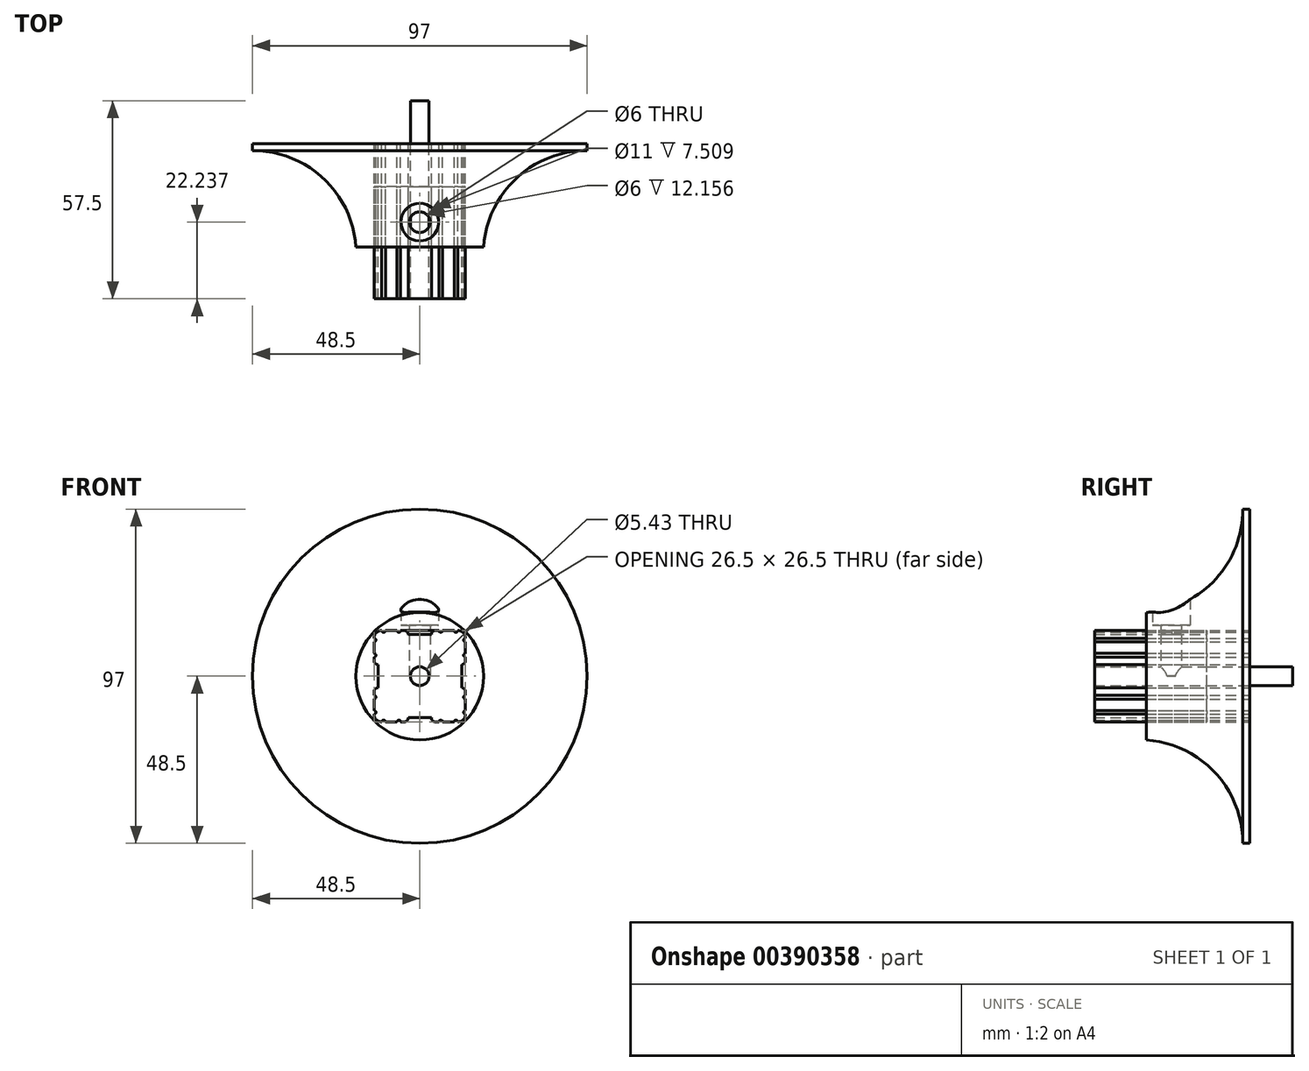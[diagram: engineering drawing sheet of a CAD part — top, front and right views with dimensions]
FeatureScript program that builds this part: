
annotation { "Feature Type Name" : "Feature", "Feature Type Description" : "" }
export const myFeature = defineFeature(function(context is Context, id is Id, definition is map)
    precondition{}
    {
        {
            var Q0;
            Q0=qCreatedBy(makeId("Front.planeOp"),FACE);
            var sketch = newSketch(context, id + "F0", { "sketchPlane" : qUnion([Q0])});
            skCircle(sketch, "E0", {"center": v(0, 0) * mm, "radius": 2.72 * mm});
            skArc(sketch, "E1", {"start": v(-1.78, -4.7) * mm, "mid": v(-3.05, -4.94) * mm, "end": v(-4.12, -5.66) * mm});
            skLineSegment(sketch, "E2", {"start": v(-1.78, -4.7) * mm, "end": v(1.78, -4.7) * mm});
            skArc(sketch, "E3", {"start": v(4.12, -5.66) * mm, "mid": v(3.05, -4.94) * mm, "end": v(1.78, -4.7) * mm});
            skLineSegment(sketch, "E4", {"start": v(4.12, -5.66) * mm, "end": v(7.5, -9.02) * mm});
            skArc(sketch, "E5", {"start": v(6.7, -10.94) * mm, "mid": v(7.74, -10.25) * mm, "end": v(7.5, -9.02) * mm});
            skLineSegment(sketch, "E6", {"start": v(6.7, -10.94) * mm, "end": v(4.47, -10.94) * mm});
            skArc(sketch, "E7", {"start": v(4.47, -10.94) * mm, "mid": v(3.7, -11.27) * mm, "end": v(3.38, -12.04) * mm});
            skLineSegment(sketch, "E8", {"start": v(3.38, -12.04) * mm, "end": v(3.38, -12.16) * mm});
            skArc(sketch, "E9", {"start": v(3.38, -12.16) * mm, "mid": v(3.7, -12.93) * mm, "end": v(4.47, -13.25) * mm});
            skLineSegment(sketch, "E10", {"start": v(4.47, -13.25) * mm, "end": v(5.55, -13.25) * mm});
            skArc(sketch, "E11", {"start": v(6.6, -13.25) * mm, "mid": v(6.08, -12.72) * mm, "end": v(5.55, -13.25) * mm});
            skLineSegment(sketch, "E12", {"start": v(6.6, -13.25) * mm, "end": v(9.96, -13.25) * mm});
            skArc(sketch, "E13", {"start": v(11.02, -13.25) * mm, "mid": v(10.5, -12.72) * mm, "end": v(9.96, -13.25) * mm});
            skArc(sketch, "E14", {"start": v(11.02, -13.25) * mm, "mid": v(12.6, -12.6) * mm, "end": v(13.25, -11.02) * mm});
            skArc(sketch, "E15", {"start": v(13.25, -9.96) * mm, "mid": v(12.72, -10.5) * mm, "end": v(13.25, -11.02) * mm});
            skLineSegment(sketch, "E16", {"start": v(13.25, -9.96) * mm, "end": v(13.25, -6.6) * mm});
            skArc(sketch, "E17", {"start": v(13.25, -5.55) * mm, "mid": v(12.72, -6.08) * mm, "end": v(13.25, -6.6) * mm});
            skLineSegment(sketch, "E18", {"start": v(13.25, -5.55) * mm, "end": v(13.25, -4.47) * mm});
            skArc(sketch, "E19", {"start": v(13.25, -4.47) * mm, "mid": v(12.93, -3.7) * mm, "end": v(12.16, -3.38) * mm});
            skLineSegment(sketch, "E20", {"start": v(12.16, -3.38) * mm, "end": v(12.04, -3.38) * mm});
            skArc(sketch, "E21", {"start": v(12.04, -3.38) * mm, "mid": v(11.27, -3.7) * mm, "end": v(10.94, -4.47) * mm});
            skLineSegment(sketch, "E22", {"start": v(10.94, -4.47) * mm, "end": v(10.94, -6.68) * mm});
            skArc(sketch, "E23", {"start": v(9.12, -7.44) * mm, "mid": v(10.28, -7.67) * mm, "end": v(10.94, -6.68) * mm});
            skLineSegment(sketch, "E24", {"start": v(9.12, -7.44) * mm, "end": v(5.68, -4) * mm});
            skArc(sketch, "E25", {"start": v(4.7, -1.66) * mm, "mid": v(4.96, -2.93) * mm, "end": v(5.68, -4) * mm});
            skLineSegment(sketch, "E26", {"start": v(4.7, -1.66) * mm, "end": v(4.7, 1.66) * mm});
            skArc(sketch, "E27", {"start": v(5.68, 4) * mm, "mid": v(4.96, 2.93) * mm, "end": v(4.7, 1.66) * mm});
            skLineSegment(sketch, "E28", {"start": v(5.68, 4) * mm, "end": v(9.12, 7.44) * mm});
            skArc(sketch, "E29", {"start": v(10.94, 6.68) * mm, "mid": v(10.28, 7.67) * mm, "end": v(9.12, 7.44) * mm});
            skLineSegment(sketch, "E30", {"start": v(10.94, 6.68) * mm, "end": v(10.94, 4.47) * mm});
            skArc(sketch, "E31", {"start": v(10.94, 4.47) * mm, "mid": v(11.27, 3.7) * mm, "end": v(12.04, 3.38) * mm});
            skLineSegment(sketch, "E32", {"start": v(12.04, 3.38) * mm, "end": v(12.16, 3.38) * mm});
            skArc(sketch, "E33", {"start": v(12.16, 3.38) * mm, "mid": v(12.93, 3.7) * mm, "end": v(13.25, 4.47) * mm});
            skLineSegment(sketch, "E34", {"start": v(13.25, 4.47) * mm, "end": v(13.25, 5.55) * mm});
            skArc(sketch, "E35", {"start": v(13.25, 6.6) * mm, "mid": v(12.72, 6.08) * mm, "end": v(13.25, 5.55) * mm});
            skLineSegment(sketch, "E36", {"start": v(13.25, 6.6) * mm, "end": v(13.25, 9.96) * mm});
            skArc(sketch, "E37", {"start": v(13.25, 11.02) * mm, "mid": v(12.72, 10.5) * mm, "end": v(13.25, 9.96) * mm});
            skArc(sketch, "E38", {"start": v(13.25, 11.02) * mm, "mid": v(12.6, 12.6) * mm, "end": v(11.02, 13.25) * mm});
            skArc(sketch, "E39", {"start": v(9.96, 13.25) * mm, "mid": v(10.5, 12.72) * mm, "end": v(11.02, 13.25) * mm});
            skLineSegment(sketch, "E40", {"start": v(9.96, 13.25) * mm, "end": v(6.6, 13.25) * mm});
            skArc(sketch, "E41", {"start": v(5.55, 13.25) * mm, "mid": v(6.08, 12.72) * mm, "end": v(6.6, 13.25) * mm});
            skLineSegment(sketch, "E42", {"start": v(5.55, 13.25) * mm, "end": v(4.47, 13.25) * mm});
            skArc(sketch, "E43", {"start": v(4.47, 13.25) * mm, "mid": v(3.7, 12.93) * mm, "end": v(3.38, 12.16) * mm});
            skLineSegment(sketch, "E44", {"start": v(3.38, 12.16) * mm, "end": v(3.38, 12.04) * mm});
            skArc(sketch, "E45", {"start": v(3.38, 12.04) * mm, "mid": v(3.7, 11.27) * mm, "end": v(4.47, 10.94) * mm});
            skLineSegment(sketch, "E46", {"start": v(4.47, 10.94) * mm, "end": v(6.76, 10.94) * mm});
            skArc(sketch, "E47", {"start": v(7.52, 9.1) * mm, "mid": v(7.75, 10.28) * mm, "end": v(6.76, 10.94) * mm});
            skLineSegment(sketch, "E48", {"start": v(7.52, 9.1) * mm, "end": v(4.07, 5.66) * mm});
            skArc(sketch, "E49", {"start": v(1.73, 4.7) * mm, "mid": v(3, 4.94) * mm, "end": v(4.07, 5.66) * mm});
            skLineSegment(sketch, "E50", {"start": v(1.73, 4.7) * mm, "end": v(-1.73, 4.7) * mm});
            skArc(sketch, "E51", {"start": v(-4.07, 5.66) * mm, "mid": v(-3, 4.94) * mm, "end": v(-1.73, 4.7) * mm});
            skLineSegment(sketch, "E52", {"start": v(-4.07, 5.66) * mm, "end": v(-7.52, 9.1) * mm});
            skArc(sketch, "E53", {"start": v(-6.76, 10.94) * mm, "mid": v(-7.75, 10.28) * mm, "end": v(-7.52, 9.1) * mm});
            skLineSegment(sketch, "E54", {"start": v(-6.76, 10.94) * mm, "end": v(-4.47, 10.94) * mm});
            skArc(sketch, "E55", {"start": v(-4.47, 10.94) * mm, "mid": v(-3.7, 11.27) * mm, "end": v(-3.38, 12.04) * mm});
            skLineSegment(sketch, "E56", {"start": v(-3.38, 12.04) * mm, "end": v(-3.38, 12.16) * mm});
            skArc(sketch, "E57", {"start": v(-3.38, 12.16) * mm, "mid": v(-3.7, 12.93) * mm, "end": v(-4.47, 13.25) * mm});
            skLineSegment(sketch, "E58", {"start": v(-4.47, 13.25) * mm, "end": v(-5.55, 13.25) * mm});
            skArc(sketch, "E59", {"start": v(-6.6, 13.25) * mm, "mid": v(-6.08, 12.72) * mm, "end": v(-5.55, 13.25) * mm});
            skLineSegment(sketch, "E60", {"start": v(-6.6, 13.25) * mm, "end": v(-9.96, 13.25) * mm});
            skArc(sketch, "E61", {"start": v(-11.02, 13.25) * mm, "mid": v(-10.5, 12.72) * mm, "end": v(-9.96, 13.25) * mm});
            skArc(sketch, "E62", {"start": v(-11.02, 13.25) * mm, "mid": v(-12.6, 12.6) * mm, "end": v(-13.25, 11.02) * mm});
            skArc(sketch, "E63", {"start": v(-13.25, 9.96) * mm, "mid": v(-12.72, 10.5) * mm, "end": v(-13.25, 11.02) * mm});
            skLineSegment(sketch, "E64", {"start": v(-13.25, 9.96) * mm, "end": v(-13.25, 6.6) * mm});
            skArc(sketch, "E65", {"start": v(-13.25, 5.55) * mm, "mid": v(-12.72, 6.08) * mm, "end": v(-13.25, 6.6) * mm});
            skLineSegment(sketch, "E66", {"start": v(-13.25, 5.55) * mm, "end": v(-13.25, 4.47) * mm});
            skArc(sketch, "E67", {"start": v(-13.25, 4.47) * mm, "mid": v(-12.93, 3.7) * mm, "end": v(-12.16, 3.38) * mm});
            skLineSegment(sketch, "E68", {"start": v(-12.16, 3.38) * mm, "end": v(-12.04, 3.38) * mm});
            skArc(sketch, "E69", {"start": v(-12.04, 3.38) * mm, "mid": v(-11.27, 3.7) * mm, "end": v(-10.94, 4.47) * mm});
            skLineSegment(sketch, "E70", {"start": v(-10.94, 4.47) * mm, "end": v(-10.94, 6.68) * mm});
            skArc(sketch, "E71", {"start": v(-9.12, 7.44) * mm, "mid": v(-10.28, 7.67) * mm, "end": v(-10.94, 6.68) * mm});
            skLineSegment(sketch, "E72", {"start": v(-9.12, 7.44) * mm, "end": v(-5.68, 4) * mm});
            skArc(sketch, "E73", {"start": v(-4.7, 1.66) * mm, "mid": v(-4.96, 2.93) * mm, "end": v(-5.68, 4) * mm});
            skLineSegment(sketch, "E74", {"start": v(-4.7, 1.66) * mm, "end": v(-4.7, -1.66) * mm});
            skArc(sketch, "E75", {"start": v(-5.68, -4) * mm, "mid": v(-4.96, -2.93) * mm, "end": v(-4.7, -1.66) * mm});
            skLineSegment(sketch, "E76", {"start": v(-5.68, -4) * mm, "end": v(-9.12, -7.44) * mm});
            skArc(sketch, "E77", {"start": v(-10.94, -6.68) * mm, "mid": v(-10.28, -7.67) * mm, "end": v(-9.12, -7.44) * mm});
            skLineSegment(sketch, "E78", {"start": v(-10.94, -6.68) * mm, "end": v(-10.94, -4.47) * mm});
            skArc(sketch, "E79", {"start": v(-10.94, -4.47) * mm, "mid": v(-11.27, -3.7) * mm, "end": v(-12.04, -3.38) * mm});
            skLineSegment(sketch, "E80", {"start": v(-12.04, -3.38) * mm, "end": v(-12.16, -3.38) * mm});
            skArc(sketch, "E81", {"start": v(-12.16, -3.38) * mm, "mid": v(-12.93, -3.7) * mm, "end": v(-13.25, -4.47) * mm});
            skLineSegment(sketch, "E82", {"start": v(-13.25, -4.47) * mm, "end": v(-13.25, -5.55) * mm});
            skArc(sketch, "E83", {"start": v(-13.25, -6.6) * mm, "mid": v(-12.72, -6.08) * mm, "end": v(-13.25, -5.55) * mm});
            skLineSegment(sketch, "E84", {"start": v(-13.25, -6.6) * mm, "end": v(-13.25, -9.96) * mm});
            skArc(sketch, "E85", {"start": v(-13.25, -11.02) * mm, "mid": v(-12.72, -10.5) * mm, "end": v(-13.25, -9.96) * mm});
            skArc(sketch, "E86", {"start": v(-13.25, -11.02) * mm, "mid": v(-12.6, -12.6) * mm, "end": v(-11.02, -13.25) * mm});
            skArc(sketch, "E87", {"start": v(-9.96, -13.25) * mm, "mid": v(-10.5, -12.72) * mm, "end": v(-11.02, -13.25) * mm});
            skLineSegment(sketch, "E88", {"start": v(-9.96, -13.25) * mm, "end": v(-6.6, -13.25) * mm});
            skArc(sketch, "E89", {"start": v(-5.55, -13.25) * mm, "mid": v(-6.08, -12.72) * mm, "end": v(-6.6, -13.25) * mm});
            skLineSegment(sketch, "E90", {"start": v(-5.55, -13.25) * mm, "end": v(-4.47, -13.25) * mm});
            skArc(sketch, "E91", {"start": v(-4.47, -13.25) * mm, "mid": v(-3.7, -12.93) * mm, "end": v(-3.38, -12.16) * mm});
            skLineSegment(sketch, "E92", {"start": v(-3.38, -12.16) * mm, "end": v(-3.38, -12.04) * mm});
            skArc(sketch, "E93", {"start": v(-3.38, -12.04) * mm, "mid": v(-3.7, -11.27) * mm, "end": v(-4.47, -10.94) * mm});
            skLineSegment(sketch, "E94", {"start": v(-4.47, -10.94) * mm, "end": v(-6.7, -10.94) * mm});
            skArc(sketch, "E95", {"start": v(-7.5, -9.02) * mm, "mid": v(-7.74, -10.25) * mm, "end": v(-6.7, -10.94) * mm});
            skLineSegment(sketch, "E96", {"start": v(-7.5, -9.02) * mm, "end": v(-4.12, -5.66) * mm});
            skLineSegment(sketch, "E97", {"start": v(-12.04, 3.38) * mm, "end": v(-12.04, -4.47) * mm});
            skLineSegment(sketch, "E98", {"start": v(-3.38, -12.04) * mm, "end": v(3.38, -12.04) * mm});
            skLineSegment(sketch, "E99", {"start": v(12.16, -3.38) * mm, "end": v(12.16, 3.38) * mm});
            skLineSegment(sketch, "E100", {"start": v(3.38, 12.16) * mm, "end": v(-3.38, 12.16) * mm});
            skSolve(sketch);
        }
        {
            var Q0;
            Q0=qCreatedBy(makeId("Front.planeOp"),FACE);
            var sketch = newSketch(context, id + "F1", { "sketchPlane" : qUnion([Q0])});
            skCircle(sketch, "E101", {"center": v(0, 0) * mm, "radius": 18.5 * mm});
            skCircle(sketch, "E102", {"center": v(0, 0) * mm, "radius": 48.5 * mm});
            skSolve(sketch);
        }
        {
            var Q0;
            Q0 = qSketchRegion(id + "F1", true);
            var Q1;
            Q1=makeQuery(id+"F1.imprint","IMPRINT",FACE,{"disambiguationData":[TD([[makeQuery(id+"F1.imprint","IMPRINT",EDGE,{"derivedFrom":sQuery(id+"F1.wireOp",EDGE,"E101")}),1.0]])]});
            extrude(context, id + "F2", {"entities" : qUnion([Q0, Q1]), "depth" : 2 * mm});
        }
        {
            var Q0;
            Q0=makeQuery(id+"F1.imprint","IMPRINT",FACE,{"disambiguationData":[TD([[makeQuery(id+"F1.imprint","IMPRINT",EDGE,{"derivedFrom":sQuery(id+"F1.wireOp",EDGE,"E101")}),1.0]])]});
            extrude(context, id + "F3", {"entities" : qUnion([Q0]), "operationType" : NewBodyOperationType.ADD, "depth" : 30 * mm});
        }
        {
            var Q0;
            Q0=makeQuery(id+"F3.boolean.opBoolean","INTERSECT",EDGE,{"derivedFrom":[makeQuery(id+"F2.opExtrude","CAP_FACE",FACE,{"disambiguationData":[OSD([sQuery(id+"F1.wireOp",EDGE,"E102")])],"isStart":false}),makeQuery(id+"F3.opExtrude","SWEPT_FACE",FACE,{"disambiguationData":[OSD([sQuery(id+"F1.wireOp",EDGE,"E101")])]})]});
            fillet(context, id + "F4", {"entities" : qUnion([Q0]), "radius" : 30 * mm, "tangentPropagation" : true, "allowEdgeOverflow" : false});
        }
        {
            var Q0;
            Q0=makeQuery(id+"F1.imprint","IMPRINT",FACE,{"disambiguationData":[TD([[makeQuery(id+"F1.imprint","IMPRINT",EDGE,{"derivedFrom":sQuery(id+"F1.wireOp",EDGE,"E101")}),-1.0]])]});
            var sketch = newSketch(context, id + "F5", { "sketchPlane" : qUnion([Q0])});
            skArc(sketch, "E103.0.0", {"start": v(-6.7, -10.94) * mm, "mid": v(-7.74, -10.25) * mm, "end": v(-7.5, -9.02) * mm});
            skLineSegment(sketch, "E103.0.1", {"start": v(-7.5, -9.02) * mm, "end": v(-4.12, -5.66) * mm});
            skArc(sketch, "E103.0.2", {"start": v(-4.12, -5.66) * mm, "mid": v(-3.05, -4.94) * mm, "end": v(-1.78, -4.7) * mm});
            skLineSegment(sketch, "E103.0.3", {"start": v(-1.78, -4.7) * mm, "end": v(1.78, -4.7) * mm});
            skArc(sketch, "E103.0.4", {"start": v(1.78, -4.7) * mm, "mid": v(3.05, -4.94) * mm, "end": v(4.12, -5.66) * mm});
            skLineSegment(sketch, "E103.0.5", {"start": v(4.12, -5.66) * mm, "end": v(7.5, -9.02) * mm});
            skArc(sketch, "E103.0.6", {"start": v(7.5, -9.02) * mm, "mid": v(7.74, -10.25) * mm, "end": v(6.7, -10.94) * mm});
            skLineSegment(sketch, "E103.0.7", {"start": v(6.7, -10.94) * mm, "end": v(4.47, -10.94) * mm});
            skArc(sketch, "E103.0.8", {"start": v(4.47, -10.94) * mm, "mid": v(3.7, -11.27) * mm, "end": v(3.38, -12.04) * mm});
            skLineSegment(sketch, "E103.0.9", {"start": v(3.38, -12.04) * mm, "end": v(3.38, -12.16) * mm});
            skArc(sketch, "E103.0.10", {"start": v(3.38, -12.16) * mm, "mid": v(3.7, -12.93) * mm, "end": v(4.47, -13.25) * mm});
            skLineSegment(sketch, "E103.0.11", {"start": v(4.47, -13.25) * mm, "end": v(5.55, -13.25) * mm});
            skArc(sketch, "E103.0.12", {"start": v(5.55, -13.25) * mm, "mid": v(6.08, -12.72) * mm, "end": v(6.6, -13.25) * mm});
            skLineSegment(sketch, "E103.0.13", {"start": v(6.6, -13.25) * mm, "end": v(9.96, -13.25) * mm});
            skArc(sketch, "E103.0.14", {"start": v(9.96, -13.25) * mm, "mid": v(10.5, -12.72) * mm, "end": v(11.02, -13.25) * mm});
            skArc(sketch, "E103.0.15", {"start": v(11.02, -13.25) * mm, "mid": v(12.6, -12.6) * mm, "end": v(13.25, -11.02) * mm});
            skArc(sketch, "E103.0.16", {"start": v(13.25, -11.02) * mm, "mid": v(12.72, -10.5) * mm, "end": v(13.25, -9.96) * mm});
            skLineSegment(sketch, "E103.0.17", {"start": v(13.25, -9.96) * mm, "end": v(13.25, -6.6) * mm});
            skArc(sketch, "E103.0.18", {"start": v(13.25, -6.6) * mm, "mid": v(12.72, -6.08) * mm, "end": v(13.25, -5.55) * mm});
            skLineSegment(sketch, "E103.0.19", {"start": v(13.25, -5.55) * mm, "end": v(13.25, -4.47) * mm});
            skArc(sketch, "E103.0.20", {"start": v(13.25, -4.47) * mm, "mid": v(12.93, -3.7) * mm, "end": v(12.16, -3.38) * mm});
            skLineSegment(sketch, "E103.0.21", {"start": v(12.16, -3.38) * mm, "end": v(12.04, -3.38) * mm});
            skArc(sketch, "E103.0.22", {"start": v(12.04, -3.38) * mm, "mid": v(11.27, -3.7) * mm, "end": v(10.94, -4.47) * mm});
            skLineSegment(sketch, "E103.0.23", {"start": v(10.94, -4.47) * mm, "end": v(10.94, -6.68) * mm});
            skArc(sketch, "E103.0.24", {"start": v(10.94, -6.68) * mm, "mid": v(10.28, -7.67) * mm, "end": v(9.12, -7.44) * mm});
            skLineSegment(sketch, "E103.0.25", {"start": v(9.12, -7.44) * mm, "end": v(5.68, -4) * mm});
            skArc(sketch, "E103.0.26", {"start": v(5.68, -4) * mm, "mid": v(4.96, -2.93) * mm, "end": v(4.7, -1.66) * mm});
            skLineSegment(sketch, "E103.0.27", {"start": v(4.7, -1.66) * mm, "end": v(4.7, 1.66) * mm});
            skArc(sketch, "E103.0.28", {"start": v(4.7, 1.66) * mm, "mid": v(4.96, 2.93) * mm, "end": v(5.68, 4) * mm});
            skLineSegment(sketch, "E103.0.29", {"start": v(5.68, 4) * mm, "end": v(9.12, 7.44) * mm});
            skArc(sketch, "E103.0.30", {"start": v(9.12, 7.44) * mm, "mid": v(10.28, 7.67) * mm, "end": v(10.94, 6.68) * mm});
            skLineSegment(sketch, "E103.0.31", {"start": v(10.94, 6.68) * mm, "end": v(10.94, 4.47) * mm});
            skArc(sketch, "E103.0.32", {"start": v(10.94, 4.47) * mm, "mid": v(11.27, 3.7) * mm, "end": v(12.04, 3.38) * mm});
            skLineSegment(sketch, "E103.0.33", {"start": v(12.04, 3.38) * mm, "end": v(12.16, 3.38) * mm});
            skArc(sketch, "E103.0.34", {"start": v(12.16, 3.38) * mm, "mid": v(12.93, 3.7) * mm, "end": v(13.25, 4.47) * mm});
            skLineSegment(sketch, "E103.0.35", {"start": v(13.25, 4.47) * mm, "end": v(13.25, 5.55) * mm});
            skArc(sketch, "E103.0.36", {"start": v(13.25, 5.55) * mm, "mid": v(12.72, 6.08) * mm, "end": v(13.25, 6.6) * mm});
            skLineSegment(sketch, "E103.0.37", {"start": v(13.25, 6.6) * mm, "end": v(13.25, 9.96) * mm});
            skArc(sketch, "E103.0.38", {"start": v(13.25, 9.96) * mm, "mid": v(12.72, 10.5) * mm, "end": v(13.25, 11.02) * mm});
            skArc(sketch, "E103.0.39", {"start": v(13.25, 11.02) * mm, "mid": v(12.6, 12.6) * mm, "end": v(11.02, 13.25) * mm});
            skArc(sketch, "E103.0.40", {"start": v(11.02, 13.25) * mm, "mid": v(10.5, 12.72) * mm, "end": v(9.96, 13.25) * mm});
            skLineSegment(sketch, "E103.0.41", {"start": v(9.96, 13.25) * mm, "end": v(6.6, 13.25) * mm});
            skArc(sketch, "E103.0.42", {"start": v(6.6, 13.25) * mm, "mid": v(6.08, 12.72) * mm, "end": v(5.55, 13.25) * mm});
            skLineSegment(sketch, "E103.0.43", {"start": v(5.55, 13.25) * mm, "end": v(4.47, 13.25) * mm});
            skArc(sketch, "E103.0.44", {"start": v(4.47, 13.25) * mm, "mid": v(3.7, 12.93) * mm, "end": v(3.38, 12.16) * mm});
            skLineSegment(sketch, "E103.0.45", {"start": v(3.38, 12.16) * mm, "end": v(3.38, 12.04) * mm});
            skArc(sketch, "E103.0.46", {"start": v(3.38, 12.04) * mm, "mid": v(3.7, 11.27) * mm, "end": v(4.47, 10.94) * mm});
            skLineSegment(sketch, "E103.0.47", {"start": v(4.47, 10.94) * mm, "end": v(6.76, 10.94) * mm});
            skArc(sketch, "E103.0.48", {"start": v(6.76, 10.94) * mm, "mid": v(7.75, 10.28) * mm, "end": v(7.52, 9.1) * mm});
            skLineSegment(sketch, "E103.0.49", {"start": v(7.52, 9.1) * mm, "end": v(4.07, 5.66) * mm});
            skArc(sketch, "E103.0.50", {"start": v(4.07, 5.66) * mm, "mid": v(3, 4.94) * mm, "end": v(1.73, 4.7) * mm});
            skLineSegment(sketch, "E103.0.51", {"start": v(1.73, 4.7) * mm, "end": v(-1.73, 4.7) * mm});
            skArc(sketch, "E103.0.52", {"start": v(-1.73, 4.7) * mm, "mid": v(-3, 4.94) * mm, "end": v(-4.07, 5.66) * mm});
            skLineSegment(sketch, "E103.0.53", {"start": v(-4.07, 5.66) * mm, "end": v(-7.52, 9.1) * mm});
            skArc(sketch, "E103.0.54", {"start": v(-7.52, 9.1) * mm, "mid": v(-7.75, 10.28) * mm, "end": v(-6.76, 10.94) * mm});
            skLineSegment(sketch, "E103.0.55", {"start": v(-6.76, 10.94) * mm, "end": v(-4.47, 10.94) * mm});
            skArc(sketch, "E103.0.56", {"start": v(-4.47, 10.94) * mm, "mid": v(-3.7, 11.27) * mm, "end": v(-3.38, 12.04) * mm});
            skLineSegment(sketch, "E103.0.57", {"start": v(-3.38, 12.04) * mm, "end": v(-3.38, 12.16) * mm});
            skArc(sketch, "E103.0.58", {"start": v(-3.38, 12.16) * mm, "mid": v(-3.7, 12.93) * mm, "end": v(-4.47, 13.25) * mm});
            skLineSegment(sketch, "E103.0.59", {"start": v(-4.47, 13.25) * mm, "end": v(-5.55, 13.25) * mm});
            skArc(sketch, "E103.0.60", {"start": v(-5.55, 13.25) * mm, "mid": v(-6.08, 12.72) * mm, "end": v(-6.6, 13.25) * mm});
            skLineSegment(sketch, "E103.0.61", {"start": v(-6.6, 13.25) * mm, "end": v(-9.96, 13.25) * mm});
            skArc(sketch, "E103.0.62", {"start": v(-9.96, 13.25) * mm, "mid": v(-10.5, 12.72) * mm, "end": v(-11.02, 13.25) * mm});
            skArc(sketch, "E103.0.63", {"start": v(-11.02, 13.25) * mm, "mid": v(-12.6, 12.6) * mm, "end": v(-13.25, 11.02) * mm});
            skArc(sketch, "E103.0.64", {"start": v(-13.25, 11.02) * mm, "mid": v(-12.72, 10.5) * mm, "end": v(-13.25, 9.96) * mm});
            skLineSegment(sketch, "E103.0.65", {"start": v(-13.25, 9.96) * mm, "end": v(-13.25, 6.6) * mm});
            skArc(sketch, "E103.0.66", {"start": v(-13.25, 6.6) * mm, "mid": v(-12.72, 6.08) * mm, "end": v(-13.25, 5.55) * mm});
            skLineSegment(sketch, "E103.0.67", {"start": v(-13.25, 5.55) * mm, "end": v(-13.25, 4.47) * mm});
            skArc(sketch, "E103.0.68", {"start": v(-13.25, 4.47) * mm, "mid": v(-12.93, 3.7) * mm, "end": v(-12.16, 3.38) * mm});
            skLineSegment(sketch, "E103.0.69", {"start": v(-12.16, 3.38) * mm, "end": v(-12.04, 3.38) * mm});
            skArc(sketch, "E103.0.70", {"start": v(-12.04, 3.38) * mm, "mid": v(-11.27, 3.7) * mm, "end": v(-10.94, 4.47) * mm});
            skLineSegment(sketch, "E103.0.71", {"start": v(-10.94, 4.47) * mm, "end": v(-10.94, 6.68) * mm});
            skArc(sketch, "E103.0.72", {"start": v(-10.94, 6.68) * mm, "mid": v(-10.28, 7.67) * mm, "end": v(-9.12, 7.44) * mm});
            skLineSegment(sketch, "E103.0.73", {"start": v(-9.12, 7.44) * mm, "end": v(-5.68, 4) * mm});
            skArc(sketch, "E103.0.74", {"start": v(-5.68, 4) * mm, "mid": v(-4.96, 2.93) * mm, "end": v(-4.7, 1.66) * mm});
            skLineSegment(sketch, "E103.0.75", {"start": v(-4.7, 1.66) * mm, "end": v(-4.7, -1.66) * mm});
            skArc(sketch, "E103.0.76", {"start": v(-4.7, -1.66) * mm, "mid": v(-4.96, -2.93) * mm, "end": v(-5.68, -4) * mm});
            skLineSegment(sketch, "E103.0.77", {"start": v(-5.68, -4) * mm, "end": v(-9.12, -7.44) * mm});
            skArc(sketch, "E103.0.78", {"start": v(-9.12, -7.44) * mm, "mid": v(-10.28, -7.67) * mm, "end": v(-10.94, -6.68) * mm});
            skLineSegment(sketch, "E103.0.79", {"start": v(-10.94, -6.68) * mm, "end": v(-10.94, -4.47) * mm});
            skArc(sketch, "E103.0.80", {"start": v(-10.94, -4.47) * mm, "mid": v(-11.27, -3.7) * mm, "end": v(-12.04, -3.38) * mm});
            skLineSegment(sketch, "E103.0.81", {"start": v(-12.04, -3.38) * mm, "end": v(-12.16, -3.38) * mm});
            skArc(sketch, "E103.0.82", {"start": v(-12.16, -3.38) * mm, "mid": v(-12.93, -3.7) * mm, "end": v(-13.25, -4.47) * mm});
            skLineSegment(sketch, "E103.0.83", {"start": v(-13.25, -4.47) * mm, "end": v(-13.25, -5.55) * mm});
            skArc(sketch, "E103.0.84", {"start": v(-13.25, -5.55) * mm, "mid": v(-12.72, -6.08) * mm, "end": v(-13.25, -6.6) * mm});
            skLineSegment(sketch, "E103.0.85", {"start": v(-13.25, -6.6) * mm, "end": v(-13.25, -9.96) * mm});
            skArc(sketch, "E103.0.86", {"start": v(-13.25, -9.96) * mm, "mid": v(-12.72, -10.5) * mm, "end": v(-13.25, -11.02) * mm});
            skArc(sketch, "E103.0.87", {"start": v(-13.25, -11.02) * mm, "mid": v(-12.6, -12.6) * mm, "end": v(-11.02, -13.25) * mm});
            skArc(sketch, "E103.0.88", {"start": v(-11.02, -13.25) * mm, "mid": v(-10.5, -12.72) * mm, "end": v(-9.96, -13.25) * mm});
            skLineSegment(sketch, "E103.0.89", {"start": v(-9.96, -13.25) * mm, "end": v(-6.6, -13.25) * mm});
            skArc(sketch, "E103.0.90", {"start": v(-6.6, -13.25) * mm, "mid": v(-6.08, -12.72) * mm, "end": v(-5.55, -13.25) * mm});
            skLineSegment(sketch, "E103.0.91", {"start": v(-5.55, -13.25) * mm, "end": v(-4.47, -13.25) * mm});
            skArc(sketch, "E103.0.92", {"start": v(-4.47, -13.25) * mm, "mid": v(-3.7, -12.93) * mm, "end": v(-3.38, -12.16) * mm});
            skLineSegment(sketch, "E103.0.93", {"start": v(-3.38, -12.16) * mm, "end": v(-3.38, -12.04) * mm});
            skArc(sketch, "E103.0.94", {"start": v(-3.38, -12.04) * mm, "mid": v(-3.7, -11.27) * mm, "end": v(-4.47, -10.94) * mm});
            skLineSegment(sketch, "E103.0.95", {"start": v(-4.47, -10.94) * mm, "end": v(-6.7, -10.94) * mm});
            skLineSegment(sketch, "E104", {"start": v(4.47, 13.25) * mm, "end": v(-4.47, 13.25) * mm});
            skSolve(sketch);
        }
        {
            var Q0;
            Q0 = qSketchRegion(id + "F5", true);
            var Q1;
            {var subQ1=sQuery(id+"F0.wireOp",EDGE,"E69");Q1=makeQuery(id+"F0.imprint","IMPRINT",FACE,{"disambiguationData":[TD([[makeQuery(id+"F0.imprint","IMPRINT",EDGE,{"derivedFrom":subQ1}),-1.0]])]});}
            var Q2;
            Q2=makeQuery(id+"F0.imprint","IMPRINT",FACE,{"disambiguationData":[TD([[makeQuery(id+"F0.imprint","IMPRINT",EDGE,{"derivedFrom":sQuery(id+"F0.wireOp",EDGE,"E20")}),-1.0]])]});
            var Q3;
            Q3=makeQuery(id+"F0.imprint","IMPRINT",FACE,{"disambiguationData":[TD([[makeQuery(id+"F0.imprint","IMPRINT",EDGE,{"derivedFrom":sQuery(id+"F0.wireOp",EDGE,"E1")}),1.0]])]});
            extrude(context, id + "F6", {"entities" : qUnion([Q0, Q1, Q2, Q3]), "operationType" : NewBodyOperationType.REMOVE, "depth" : 40 * mm});
        }
        {
            var Q0;
            Q0 = qSketchRegion(id + "F0", true);
            extrude(context, id + "F7", {"entities" : qUnion([Q0]), "depth" : 45 * mm});
        }
        {
            var Q0;
            Q0=qCreatedBy(makeId("Top.planeOp"),FACE);
            var sketch = newSketch(context, id + "F8", { "sketchPlane" : qUnion([Q0])});
            skCircle(sketch, "E105", {"center": v(0, -22.76) * mm, "radius": 5.5 * mm});
            skCircle(sketch, "E106", {"center": v(0, -22.76) * mm, "radius": 3 * mm});
            skSolve(sketch);
        }
        {
            var Q0;
            Q0=makeQuery(id+"F8.imprint","IMPRINT",FACE,{"disambiguationData":[TD([[makeQuery(id+"F8.imprint","IMPRINT",EDGE,{"derivedFrom":sQuery(id+"F8.wireOp",EDGE,"E106")}),1.0]])]});
            extrude(context, id + "F9", {"entities" : qUnion([Q0]), "operationType" : NewBodyOperationType.REMOVE, "depth" : 40 * mm});
        }
        {
            var Q0;
            Q0=makeQuery(id+"F8.imprint","IMPRINT",FACE,{"disambiguationData":[TD([[makeQuery(id+"F8.imprint","IMPRINT",EDGE,{"derivedFrom":sQuery(id+"F8.wireOp",EDGE,"E105")}),1.0]])]});
            extrude(context, id + "F10", {"entities" : qUnion([Q0]), "operationType" : NewBodyOperationType.REMOVE, "depth" : 25 * mm, "hasSecondDirection" : true, "secondDirectionOppositeDirection" : false, "secondDirectionDepth" : 14.8 * mm});
        }
        {
            var Q0;
            Q0=makeQuery(id+"F0.imprint","IMPRINT",FACE,{"disambiguationData":[TD([[makeQuery(id+"F0.imprint","IMPRINT",EDGE,{"derivedFrom":sQuery(id+"F0.wireOp",EDGE,"E0")}),1.0]])]});
            extrude(context, id + "F11", {"entities" : qUnion([Q0]), "endBound" : BoundingType.SYMMETRIC, "depth" : 25 * mm});
        }
        {
            var Q0;
            Q0=qSketchRegion(id+"F1",true);
            var Q1;
            Q1=makeQuery(id+"F1.imprint","IMPRINT",FACE,{"disambiguationData":[TD([[makeQuery(id+"F1.imprint","IMPRINT",EDGE,{"derivedFrom":sQuery(id+"F1.wireOp",EDGE,"E101")}),1.0]])]});
            extrude(context, id + "F12", {"entities" : qUnion([Q0, Q1]), "endBound" : BoundingType.SYMMETRIC, "depth" : 5 * mm});
        }
        {
            var Q0;
            Q0=qSketchRegion(id+"F0",true);
            extrude(context, id + "F13", {"entities" : qUnion([Q0]), "operationType" : NewBodyOperationType.REMOVE, "endBound" : BoundingType.SYMMETRIC, "oppositeDirection" : true, "depth" : 25 * mm});
        }
        {
            var Q0;
            Q0=makeQuery(id+"F13.boolean.opBoolean","SPLIT",BODY,{"disambiguationData":[OD(1.0)],"derivedFrom":makeQuery(id+"F12.opExtrude","SWEPT_BODY",BODY,{"disambiguationData":[OSD([sQuery(id+"F1.wireOp",EDGE,"E102")])]})});
            deleteBodies(context, id + "F14", {"entities" : qUnion([Q0])});
        }
    });
